# Revit family: Hager-Gamma-IP30-sistema-NoHosted-PT-pt
name_source: partatom
category: Electrical Equipment
units: mm (PartAtom-declared; Revit-internal decimal feet)

## family parameters
Always vertical = Yes
Cut with Voids When Loaded = No
Panel Configuration = Two Columns, Circuits Across
Part Type = Panelboard
Room Calculation Point = No
Round Connector Dimension = Use Diameter
Shared = No
Work Plane-Based = Yes

## types (9) — shared parameters
Default Elevation = 1219 mm
EF000003 - Método de montagem = EV000384 - Montagem em superfície (gesso)
EF000049 - Profundidade = 103 mm  [stored 0.337927 ft]
EF000116 - Número RAL = 9010
EF000339 - Tipo de difusor = EV001012 - Tampa
EF001062 - Versão EMC = No
EF001596 - Material do corpo = EV000139 - Plástico
EF004462 - Tipo de fecho = EV000154 - Outro
EF006244 - Tampa/porta transparente = No
EF006306 - Com fecho = No
HG000001 - Número de colunas = 1
HG000002 - Com porta ou tampa = No
HG000003 - Gama = Gamma
HG000005 - Espessura = 3 mm  [stored 0.00984252 ft]
HG000006 - Encastrado = No
HG000009 - Porta dupla = No
HG000010 - Portas assimétricas = No
HG000011 - Filas vazias desde da parte de baixo = No
HG000017 - Distância entre polos = 18 mm  [stored 0.0590551 ft]
Manufacturer = Hager
Type Comments = Gamma
zero-valued in all types: EF000218 - Profundidade incorporada, EF000332 - Altura embutida, EF000846 - Largura para embutir, EF001131 - Profundidade interior, HG000007 - Número de colunas vazias, HG000008 - Número de filas vazias

## per-type parameters (varying)
| type | EF000007 - Cor | EF000008 - Largura | EF000040 - Altura | EF000118 - Com tampa de montagem | EF000266 - Número de linhas | EF001088 - Extensão possível | EF001134 - Calha DIN | EF002950 - Largura em número de módulos | EF005474 - Grau de proteção (IP) | EF009212 - Tipo de tampa | EF015776 - Borne de terra | EF015777 - Borne de neutro | EF015941 - Porta para passagem de sinal | HG000004 - Referência do Fabricante | Model |
| Montagem em superfície IP30 L250 A250 P103 13 unidade de divisão - GD113B | EV000202 - Branco | 250 mm  [stored 0.82021 ft] | 250 mm  [stored 0.82021 ft] | No | 1 | Yes | Yes | 13 | EV006410 - IP30 | EV009916 - Com recuo | Yes | Yes | Yes | GD113B | GD113B |
| Montagem em superfície IP30 L250 A375 P103 13 unidade de divisão - GD213B | EV000202 - Branco | 250 mm  [stored 0.82021 ft] | 375 mm | No | 2 | Yes | Yes | 13 | EV006410 - IP30 | EV009916 - Com recuo | No | No | No | GD213B | GD213B |
| Montagem em superfície IP30 L250 A500 P103 13 unidade de divisão - GD313B | EV000202 - Branco | 250 mm  [stored 0.82021 ft] | 500 mm  [stored 1.64042 ft] | No | 3 | Yes | Yes | 13 | EV006410 - IP30 | EV009916 - Com recuo | No | No | No | GD313B | GD313B |
| Montagem em superfície IP30 L250 A625 P103 13 unidade de divisão - GD413B | EV000202 - Branco | 250 mm  [stored 0.82021 ft] | 625 mm  [stored 2.05052 ft] | No | 4 | Yes | Yes | 13 | EV006410 - IP30 | EV009916 - Com recuo | No | No | No | GD413B | GD413B |
| Montagem em superfície IP30 L355 A250 P103 18 unidade de divisão - GD118B | EV000202 - Branco | 355 mm  [stored 1.1647 ft] | 250 mm  [stored 0.82021 ft] | No | 1 | Yes | Yes | 18 | EV006410 - IP30 | EV009916 - Com recuo | No | No | No | GD118B | GD118B |
| Montagem em superfície IP30 L355 A375 P103 18 unidade de divisão - GD218B | EV000202 - Branco | 355 mm  [stored 1.1647 ft] | 375 mm | No | 2 | Yes | Yes | 18 | EV006410 - IP30 | EV009916 - Com recuo | No | No | No | GD218B | GD218B |
| Montagem em superfície IP30 L355 A500 P103 18 unidade de divisão - GD318B | EV000202 - Branco | 355 mm  [stored 1.1647 ft] | 500 mm  [stored 1.64042 ft] | Yes | 3 | Yes | Yes | 18 | EV006410 - IP30 | EV009916 - Com recuo | No | No | No | GD318B | GD318B |
| Montagem em superfície IP30 L355 A625 P103 18 unidade de divisão - GD418B | EV000202 - Branco | 355 mm  [stored 1.1647 ft] | 625 mm  [stored 2.05052 ft] | Yes | 4 | Yes | Yes | 18 | EV006410 - IP30 | EV009916 - Com recuo | No | No | No | GD418B | GD418B |
| Montagem em superfície IP40 L355 A250 P103 10 unidade de divisão - GD018A |  | 355 mm  [stored 1.1647 ft] | 250 mm  [stored 0.82021 ft] | No | 1 | No | No | 10 | EV006415 - IP40 |  | No | No | No | GD018A | GD018A |

note: [stored X ft] marks values corroborated as IEEE doubles in the binary element streams (Revit-internal decimal feet)

## geometry (parser evidence)
native form markers: Sweep x13
no freeform markers — native parametric forms only
